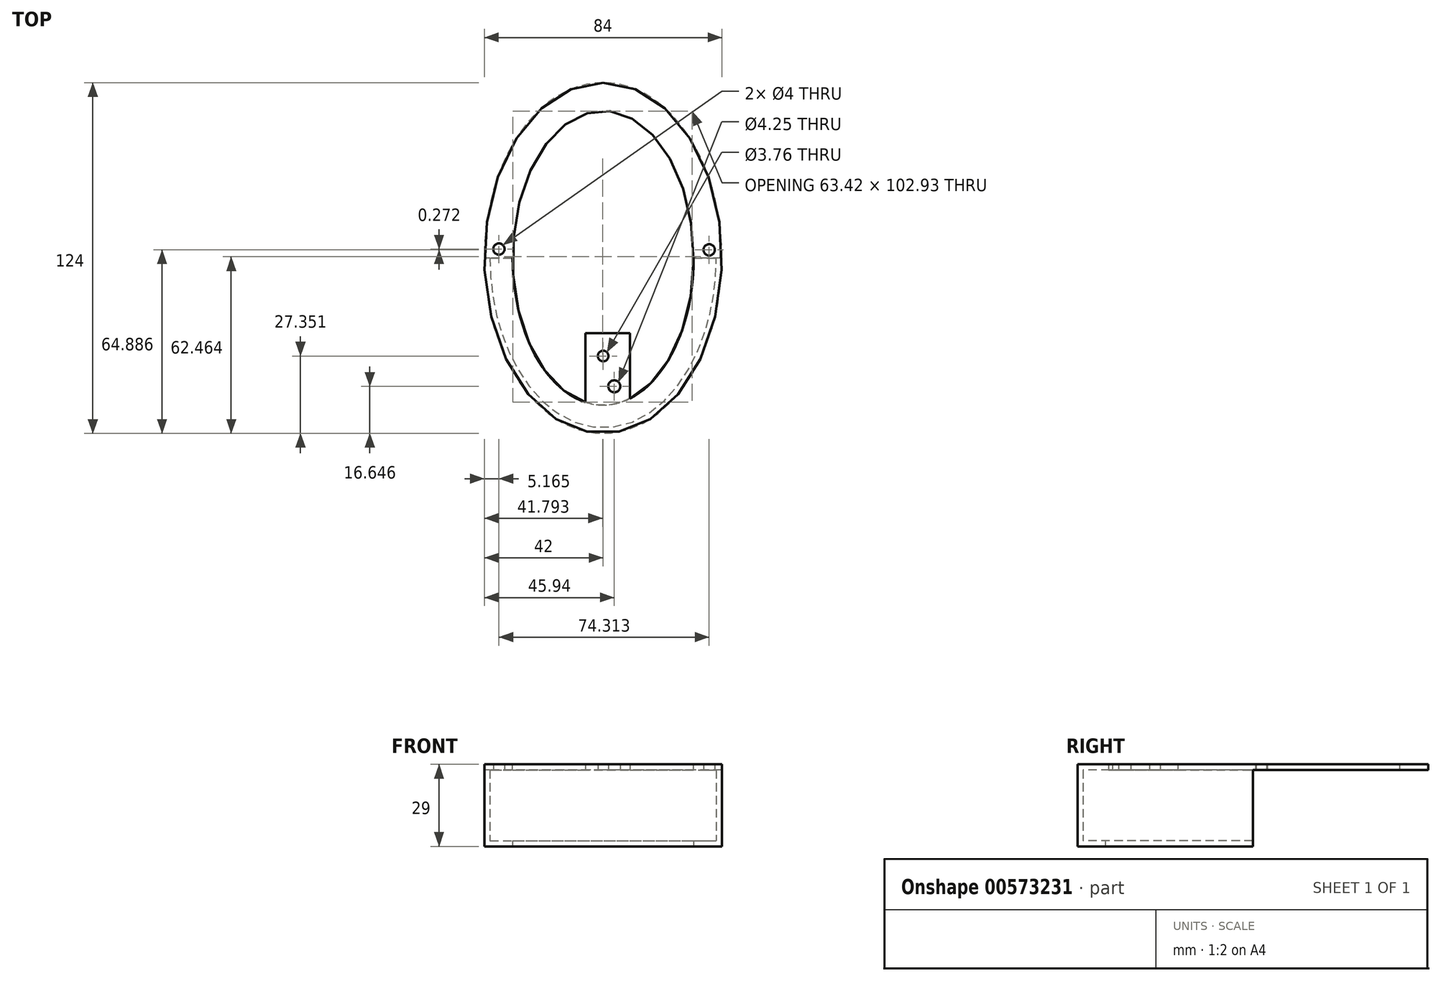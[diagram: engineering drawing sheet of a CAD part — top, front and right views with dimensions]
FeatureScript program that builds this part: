
annotation { "Feature Type Name" : "Feature", "Feature Type Description" : "" }
export const myFeature = defineFeature(function(context is Context, id is Id, definition is map)
    precondition{}
    {
        {
            var Q0;
            Q0=qCreatedBy(makeId("Top.planeOp"),FACE);
            var sketch = newSketch(context, id + "F0", { "sketchPlane" : qUnion([Q0])});
            skEllipse(sketch, "E0", {"center": v(0, 0) * mm, "majorRadius": 62 * mm, "minorRadius": 42 * mm, "majorAxis": v(0, 1)});
            skEllipse(sketch, "E1", {"center": v(0, 0) * mm, "majorRadius": 52 * mm, "minorRadius": 32 * mm, "majorAxis": v(0, 1)});
            skSolve(sketch);
        }
        {
            var Q0;
            Q0 = qSketchRegion(id + "F0", true);
            extrude(context, id + "F1", {"entities" : qUnion([Q0]), "depth" : 29 * mm, "offsetDistance" : 25 * mm});
        }
        {
            var Q0;
            Q0=makeQuery(id+"F1.opExtrude","SWEPT_FACE",FACE,{"disambiguationData":[OSD([sQuery(id+"F0.wireOp",EDGE,"E1")])]});
            shell(context, id + "F2", {"entities" : qUnion([Q0]), "thickness" : 2 * mm});
        }
        {
            var Q0;
            Q0=qCreatedBy(makeId("Top.planeOp"),FACE);
            var sketch = newSketch(context, id + "F3", { "sketchPlane" : qUnion([Q0])});
            skLineSegment(sketch, "E2.bottom", {"start": v(52.1, 66.32) * mm, "end": v(-60.1, 66.32) * mm});
            skLineSegment(sketch, "E2.top", {"start": v(52.1, 0) * mm, "end": v(-60.1, 0) * mm});
            skLineSegment(sketch, "E2.left", {"start": v(52.1, 66.32) * mm, "end": v(52.1, 0) * mm});
            skLineSegment(sketch, "E2.right", {"start": v(-60.1, 66.32) * mm, "end": v(-60.1, 0) * mm});
            skSolve(sketch);
        }
        {
            var Q0;
            Q0 = qSketchRegion(id + "F3", true);
            extrude(context, id + "F4", {"entities" : qUnion([Q0]), "operationType" : NewBodyOperationType.REMOVE, "depth" : 27 * mm, "offsetDistance" : 25 * mm});
        }
        {
            var Q0;
            {var subQ0=sQuery(id+"F0.wireOp",EDGE,"E1");var subQ1=sQuery(id+"F0.wireOp",EDGE,"E0");Q0=makeQuery(id+"F4.boolean.opBoolean","MERGE",FACE,{"derivedFrom":[makeQuery(id+"F2.opShell","OFFSET_FACE",FACE,{"disambiguationData":[OSD([subQ1,subQ0]),TDD([makeQuery(id+"F1.opExtrude","CAP_FACE",FACE,{"disambiguationData":[OSD([subQ1,subQ0])],"isStart":false})])]}),makeQuery(id+"F4.opExtrude","CAP_FACE",FACE,{"disambiguationData":[OSD([sQuery(id+"F3.wireOp",EDGE,"E2.bottom"),sQuery(id+"F3.wireOp",EDGE,"E2.top"),sQuery(id+"F3.wireOp",EDGE,"E2.left"),sQuery(id+"F3.wireOp",EDGE,"E2.right")])],"isStart":false})]});}
            var sketch = newSketch(context, id + "F5", { "sketchPlane" : qUnion([Q0])});
            skLineSegment(sketch, "E3.bottom", {"start": v(9.48, 52.96) * mm, "end": v(-6.24, 52.96) * mm});
            skLineSegment(sketch, "E3.top", {"start": v(9.48, 26.55) * mm, "end": v(-6.24, 26.55) * mm});
            skLineSegment(sketch, "E3.left", {"start": v(9.48, 52.96) * mm, "end": v(9.48, 26.55) * mm});
            skLineSegment(sketch, "E3.right", {"start": v(-6.24, 52.96) * mm, "end": v(-6.24, 26.55) * mm});
            skSolve(sketch);
        }
        {
            var Q0;
            Q0 = qSketchRegion(id + "F5", true);
            extrude(context, id + "F6", {"entities" : qUnion([Q0]), "operationType" : NewBodyOperationType.ADD, "oppositeDirection" : true, "depth" : 2 * mm, "offsetDistance" : 25 * mm});
        }
        {
            var Q0;
            {var subQ0=sQuery(id+"F0.wireOp",EDGE,"E1");var subQ1=sQuery(id+"F0.wireOp",EDGE,"E0");Q0=makeQuery(id+"F6.boolean.opBoolean","MERGE",FACE,{"derivedFrom":[makeQuery(id+"F4.boolean.opBoolean","MERGE",FACE,{"derivedFrom":[makeQuery(id+"F2.opShell","OFFSET_FACE",FACE,{"disambiguationData":[OSD([subQ1,subQ0]),TDD([makeQuery(id+"F1.opExtrude","CAP_FACE",FACE,{"disambiguationData":[OSD([subQ1,subQ0])],"isStart":false})])]}),makeQuery(id+"F4.opExtrude","CAP_FACE",FACE,{"disambiguationData":[OSD([sQuery(id+"F3.wireOp",EDGE,"E2.bottom"),sQuery(id+"F3.wireOp",EDGE,"E2.top"),sQuery(id+"F3.wireOp",EDGE,"E2.left"),sQuery(id+"F3.wireOp",EDGE,"E2.right")])],"isStart":false})]}),makeQuery(id+"F6.opExtrude","CAP_FACE",FACE,{"disambiguationData":[OSD([sQuery(id+"F5.wireOp",EDGE,"E3.bottom"),sQuery(id+"F5.wireOp",EDGE,"E3.top"),sQuery(id+"F5.wireOp",EDGE,"E3.left"),sQuery(id+"F5.wireOp",EDGE,"E3.right")])],"isStart":true})]});}
            var sketch = newSketch(context, id + "F7", { "sketchPlane" : qUnion([Q0])});
            skCircle(sketch, "E4", {"center": v(37.48, -2.89) * mm, "radius": 2 * mm});
            skSolve(sketch);
        }
        {
            var Q0;
            Q0 = qSketchRegion(id + "F7", true);
            var Q1;
            Q1=makeQuery(id+"F7.imprint","IMPRINT",FACE,{"disambiguationData":[TD([[makeQuery(id+"F7.imprint","IMPRINT",EDGE,{"derivedFrom":makeQuery(id+"F6.opExtrude","CAP_EDGE",EDGE,{"disambiguationData":[OSD([sQuery(id+"F5.wireOp",EDGE,"E3.top")])],"isStart":true})}),1.0]])]});
            extrude(context, id + "F8", {"entities" : qUnion([Q0, Q1]), "operationType" : NewBodyOperationType.REMOVE, "oppositeDirection" : true, "depth" : 5 * mm, "offsetDistance" : 25 * mm});
        }
        {
            var Q0;
            {var subQ0=sQuery(id+"F0.wireOp",EDGE,"E1");var subQ1=sQuery(id+"F0.wireOp",EDGE,"E0");Q0=makeQuery(id+"F6.boolean.opBoolean","MERGE",FACE,{"derivedFrom":[makeQuery(id+"F4.boolean.opBoolean","MERGE",FACE,{"derivedFrom":[makeQuery(id+"F2.opShell","OFFSET_FACE",FACE,{"disambiguationData":[OSD([subQ1,subQ0]),TDD([makeQuery(id+"F1.opExtrude","CAP_FACE",FACE,{"disambiguationData":[OSD([subQ1,subQ0])],"isStart":false})])]}),makeQuery(id+"F4.opExtrude","CAP_FACE",FACE,{"disambiguationData":[OSD([sQuery(id+"F3.wireOp",EDGE,"E2.bottom"),sQuery(id+"F3.wireOp",EDGE,"E2.top"),sQuery(id+"F3.wireOp",EDGE,"E2.left"),sQuery(id+"F3.wireOp",EDGE,"E2.right")])],"isStart":false})]}),makeQuery(id+"F6.opExtrude","CAP_FACE",FACE,{"disambiguationData":[OSD([sQuery(id+"F5.wireOp",EDGE,"E3.bottom"),sQuery(id+"F5.wireOp",EDGE,"E3.top"),sQuery(id+"F5.wireOp",EDGE,"E3.left"),sQuery(id+"F5.wireOp",EDGE,"E3.right")])],"isStart":true})]});}
            var sketch = newSketch(context, id + "F9", { "sketchPlane" : qUnion([Q0])});
            skCircle(sketch, "E5", {"center": v(-36.84, -3.16) * mm, "radius": 2 * mm});
            skSolve(sketch);
        }
        {
            var Q0;
            Q0 = qSketchRegion(id + "F9", true);
            var Q1;
            Q1=makeQuery(id+"F9.imprint","IMPRINT",FACE,{"disambiguationData":[TD([[makeQuery(id+"F9.imprint","IMPRINT",EDGE,{"derivedFrom":makeQuery(id+"F6.opExtrude","CAP_EDGE",EDGE,{"disambiguationData":[OSD([sQuery(id+"F5.wireOp",EDGE,"E3.top")])],"isStart":true})}),1.0]])]});
            extrude(context, id + "F10", {"entities" : qUnion([Q0, Q1]), "operationType" : NewBodyOperationType.REMOVE, "oppositeDirection" : true, "depth" : 5 * mm, "offsetDistance" : 25 * mm});
        }
        {
            var Q0;
            Q0=qCreatedBy(makeId("Top.planeOp"),FACE);
            var sketch = newSketch(context, id + "F11", { "sketchPlane" : qUnion([Q0])});
            skCircle(sketch, "E6", {"center": v(0, -34.65) * mm, "radius": 1.88 * mm});
            skCircle(sketch, "E7", {"center": v(3.94, -45.35) * mm, "radius": 2.13 * mm});
            skSolve(sketch);
        }
        {
            var Q0;
            Q0 = qSketchRegion(id + "F11", true);
            extrude(context, id + "F12", {"entities" : qUnion([Q0]), "operationType" : NewBodyOperationType.REMOVE, "depth" : 40 * mm, "offsetDistance" : 25 * mm});
        }
    });
